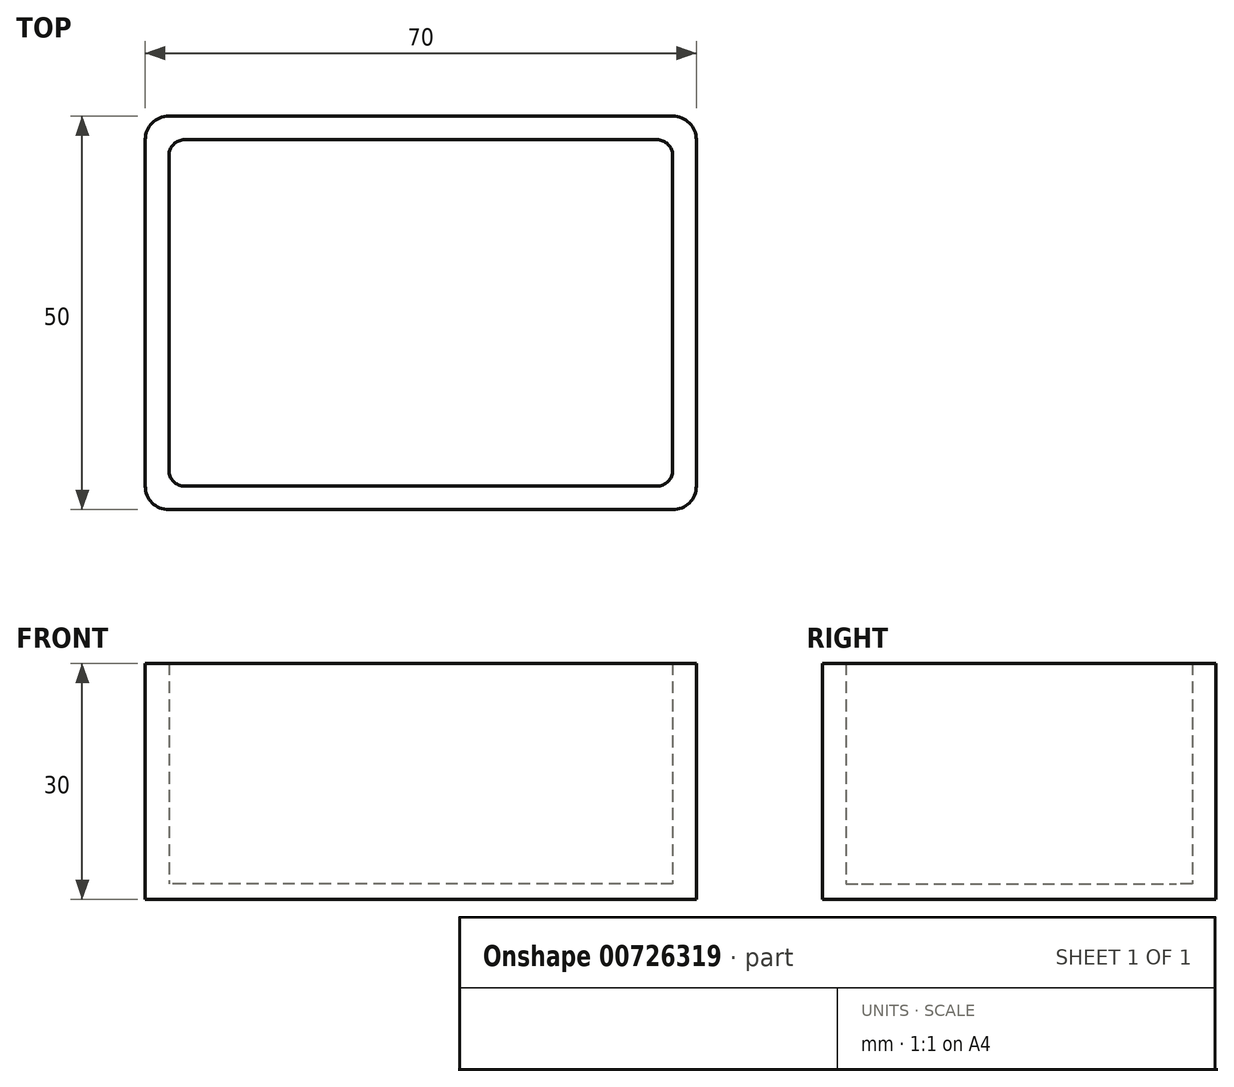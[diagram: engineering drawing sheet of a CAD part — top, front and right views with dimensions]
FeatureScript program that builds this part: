
annotation { "Feature Type Name" : "Feature", "Feature Type Description" : "" }
export const myFeature = defineFeature(function(context is Context, id is Id, definition is map)
    precondition{}
    {
        {
            var Q0;
            Q0=qCreatedBy(makeId("Top.planeOp"),FACE);
            var sketch = newSketch(context, id + "F0", { "sketchPlane" : qUnion([Q0])});
            skLineSegment(sketch, "E0.bottom", {"start": v(32, -25) * mm, "end": v(-32, -25) * mm});
            skLineSegment(sketch, "E0.top", {"start": v(32, 25) * mm, "end": v(-32, 25) * mm});
            skLineSegment(sketch, "E0.left", {"start": v(35, -22) * mm, "end": v(35, 22) * mm});
            skLineSegment(sketch, "E0.right", {"start": v(-35, -22) * mm, "end": v(-35, 22) * mm});
            skPoint(sketch, "E0.middle", {"position": v(0, 0) * mm});
            skPoint(sketch, "E1.visualSharp", {"position": v(-35, 25) * mm});
            skArc(sketch, "E1.filletArc", {"start": v(-32, 25) * mm, "mid": v(-34.12, 24.12) * mm, "end": v(-35, 22) * mm});
            skPoint(sketch, "E2.visualSharp", {"position": v(-35, -25) * mm});
            skArc(sketch, "E2.filletArc", {"start": v(-35, -22) * mm, "mid": v(-34.12, -24.12) * mm, "end": v(-32, -25) * mm});
            skPoint(sketch, "E3.visualSharp", {"position": v(35, 25) * mm});
            skArc(sketch, "E3.filletArc", {"start": v(35, 22) * mm, "mid": v(34.12, 24.12) * mm, "end": v(32, 25) * mm});
            skPoint(sketch, "E4.visualSharp", {"position": v(35, -25) * mm});
            skArc(sketch, "E4.filletArc", {"start": v(32, -25) * mm, "mid": v(34.12, -24.12) * mm, "end": v(35, -22) * mm});
            skLineSegment(sketch, "E5.0", {"start": v(-32, -20) * mm, "end": v(-32, 20) * mm});
            skLineSegment(sketch, "E5.1", {"start": v(30, -22) * mm, "end": v(-30, -22) * mm});
            skLineSegment(sketch, "E5.2", {"start": v(32, -20) * mm, "end": v(32, 20) * mm});
            skLineSegment(sketch, "E5.3", {"start": v(30, 22) * mm, "end": v(-30, 22) * mm});
            skArc(sketch, "E6.filletArc", {"start": v(32, 20) * mm, "mid": v(31.41, 21.41) * mm, "end": v(30, 22) * mm});
            skArc(sketch, "E7.filletArc", {"start": v(-30, 22) * mm, "mid": v(-31.41, 21.41) * mm, "end": v(-32, 20) * mm});
            skArc(sketch, "E8.filletArc", {"start": v(-32, -20) * mm, "mid": v(-31.41, -21.41) * mm, "end": v(-30, -22) * mm});
            skArc(sketch, "E9.filletArc", {"start": v(30, -22) * mm, "mid": v(31.41, -21.41) * mm, "end": v(32, -20) * mm});
            skSolve(sketch);
        }
        {
            var Q0;
            Q0=makeQuery(id+"F0.imprint","IMPRINT",FACE,{"disambiguationData":[TD([[makeQuery(id+"F0.imprint","IMPRINT",EDGE,{"derivedFrom":sQuery(id+"F0.wireOp",EDGE,"E0.bottom")}),-1.0]])]});
            extrude(context, id + "F1", {"entities" : qUnion([Q0]), "depth" : 30 * mm, "offsetDistance" : 25 * mm});
        }
        {
            var Q0;
            Q0=makeQuery(id+"F0.imprint","IMPRINT",FACE,{"disambiguationData":[TD([[makeQuery(id+"F0.imprint","IMPRINT",EDGE,{"derivedFrom":sQuery(id+"F0.wireOp",EDGE,"E5.0")}),-1.0]])]});
            extrude(context, id + "F2", {"entities" : qUnion([Q0]), "operationType" : NewBodyOperationType.ADD, "depth" : 2 * mm, "offsetDistance" : 25 * mm});
        }
    });
